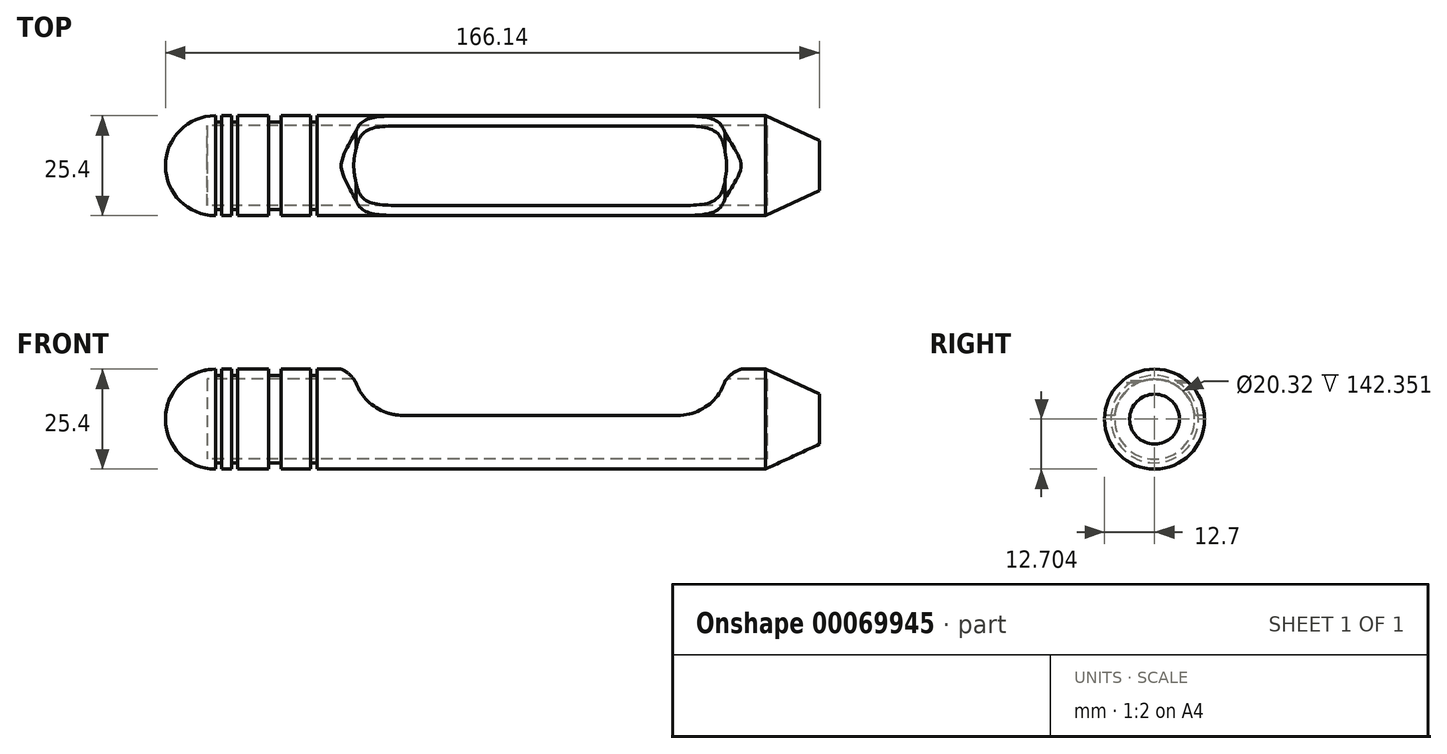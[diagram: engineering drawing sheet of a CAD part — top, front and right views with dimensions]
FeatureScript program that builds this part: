
annotation { "Feature Type Name" : "Feature", "Feature Type Description" : "" }
export const myFeature = defineFeature(function(context is Context, id is Id, definition is map)
    precondition{}
    {
        {
            var Q0;
            Q0=qCreatedBy(makeId("Front.planeOp"),FACE);
            var sketch = newSketch(context, id + "F0", { "sketchPlane" : qUnion([Q0])});
            skLineSegment(sketch, "E0", {"start": v(-86.56, 11.72) * mm, "end": v(-78.7, 11.72) * mm});
            skLineSegment(sketch, "E1", {"start": v(-78.7, 11.72) * mm, "end": v(-78.7, 10.14) * mm});
            skLineSegment(sketch, "E2", {"start": v(-78.7, 10.14) * mm, "end": v(-75.52, 10.14) * mm});
            skLineSegment(sketch, "E3", {"start": v(-75.52, 10.14) * mm, "end": v(-75.52, 11.72) * mm});
            skLineSegment(sketch, "E4", {"start": v(-75.52, 11.72) * mm, "end": v(-67.99, 11.72) * mm});
            skLineSegment(sketch, "E5", {"start": v(-67.99, 11.72) * mm, "end": v(-67.99, 10.14) * mm});
            skLineSegment(sketch, "E6", {"start": v(-67.99, 10.14) * mm, "end": v(-66.4, 10.14) * mm});
            skLineSegment(sketch, "E7", {"start": v(-66.4, 10.14) * mm, "end": v(-66.4, 11.72) * mm});
            skLineSegment(sketch, "E8", {"start": v(-66.4, 11.72) * mm, "end": v(47.46, 11.72) * mm});
            skLineSegment(sketch, "E9", {"start": v(47.46, 11.72) * mm, "end": v(47.46, -0.98) * mm, "construction": true});
            skLineSegment(sketch, "E10", {"start": v(-92.24, -0.98) * mm, "end": v(-92.24, 11.72) * mm, "construction": true});
            skLineSegment(sketch, "E11", {"start": v(-88.14, 11.72) * mm, "end": v(-88.14, 10.14) * mm});
            skLineSegment(sketch, "E12", {"start": v(-88.14, 10.14) * mm, "end": v(-86.56, 10.14) * mm});
            skLineSegment(sketch, "E13", {"start": v(-86.56, 10.14) * mm, "end": v(-86.56, 11.72) * mm});
            skLineSegment(sketch, "E14", {"start": v(47.46, -0.98) * mm, "end": v(-104.94, -0.98) * mm});
            skArc(sketch, "E15", {"start": v(-92.24, 11.72) * mm, "mid": v(-101.22, 8) * mm, "end": v(-104.94, -0.98) * mm});
            skLineSegment(sketch, "E16", {"start": v(-92.24, 11.72) * mm, "end": v(-92.24, 10.14) * mm});
            skLineSegment(sketch, "E17", {"start": v(-92.24, 10.14) * mm, "end": v(-90.65, 10.14) * mm});
            skLineSegment(sketch, "E18", {"start": v(-90.65, 10.14) * mm, "end": v(-90.65, 11.72) * mm});
            skLineSegment(sketch, "E19", {"start": v(-90.65, 11.72) * mm, "end": v(-88.14, 11.72) * mm});
            skLineSegment(sketch, "E20", {"start": v(61.2, 5.37) * mm, "end": v(61.2, -0.98) * mm});
            skLineSegment(sketch, "E21", {"start": v(47.46, 11.72) * mm, "end": v(61.2, 5.37) * mm});
            skLineSegment(sketch, "E22", {"start": v(61.2, -0.98) * mm, "end": v(47.46, -0.98) * mm});
            skSolve(sketch);
        }
        {
            var Q0;
            Q0 = qSketchRegion(id + "F0", true);
            var Q1;
            Q1=sQuery(id+"F0.wireOp",EDGE,"E14");
            revolve(context, id + "F1", {"entities" : qUnion([Q0]), "axis" : qUnion([Q1]), "revolveType" : RevolveType.FULL});
        }
        {
            var Q0;
            Q0=qCreatedBy(makeId("Front.planeOp"),FACE);
            var sketch = newSketch(context, id + "F2", { "sketchPlane" : qUnion([Q0])});
            skLineSegment(sketch, "E23", {"start": v(-44.62, 0) * mm, "end": v(25.23, 0) * mm});
            skArc(sketch, "E24", {"start": v(-56.53, 8.29) * mm, "mid": v(-58.1, 10.33) * mm, "end": v(-60.27, 11.72) * mm});
            skArc(sketch, "E25", {"start": v(41.33, 11.72) * mm, "mid": v(39.04, 10.54) * mm, "end": v(37.27, 8.67) * mm});
            skArc(sketch, "E26", {"start": v(-56.53, 8.29) * mm, "mid": v(-51.87, 2.28) * mm, "end": v(-44.62, 0) * mm});
            skArc(sketch, "E27", {"start": v(25.23, 0) * mm, "mid": v(32.65, 2.4) * mm, "end": v(37.27, 8.67) * mm});
            skLineSegment(sketch, "E28.0", {"start": v(-66.4, 11.72) * mm, "end": v(-66.4, -13.68) * mm});
            skLineSegment(sketch, "E29", {"start": v(-66.4, 11.72) * mm, "end": v(-60.27, 11.72) * mm});
            skLineSegment(sketch, "E30", {"start": v(-60.27, 11.72) * mm, "end": v(41.33, 11.72) * mm});
            skLineSegment(sketch, "E31.0", {"start": v(47.46, 11.72) * mm, "end": v(47.46, -13.68) * mm});
            skLineSegment(sketch, "E32", {"start": v(41.33, 11.72) * mm, "end": v(47.46, 11.72) * mm});
            skSolve(sketch);
        }
        {
            var Q0;
            Q0 = qSketchRegion(id + "F2", true);
            extrude(context, id + "F3", {"entities" : qUnion([Q0]), "operationType" : NewBodyOperationType.REMOVE, "endBound" : BoundingType.SYMMETRIC, "oppositeDirection" : true, "depth" : 25.4 * mm});
        }
        {
            var Q0;
            Q0=makeQuery(id+"F1.opRevolve","SWEPT_FACE",FACE,{"disambiguationData":[OSD([sQuery(id+"F0.wireOp",EDGE,"E18")])]});
            var sketch = newSketch(context, id + "F4", { "sketchPlane" : qUnion([Q0])});
            skCircle(sketch, "E33", {"center": v(0, -0.98) * mm, "radius": 10.16 * mm});
            skSolve(sketch);
        }
        {
            var Q0;
            Q0=makeQuery(id+"F4.imprint","IMPRINT",FACE,{"disambiguationData":[TD([[makeQuery(id+"F4.imprint","IMPRINT",EDGE,{"derivedFrom":sQuery(id+"F4.wireOp",EDGE,"E33")}),1.0]])]});
            extrude(context, id + "F5", {"entities" : qUnion([Q0]), "operationType" : NewBodyOperationType.REMOVE, "oppositeDirection" : true, "depth" : 138.6 * mm, "hasSecondDirection" : true, "secondDirectionOppositeDirection" : false, "secondDirectionDepth" : 3.74 * mm});
        }
    });
